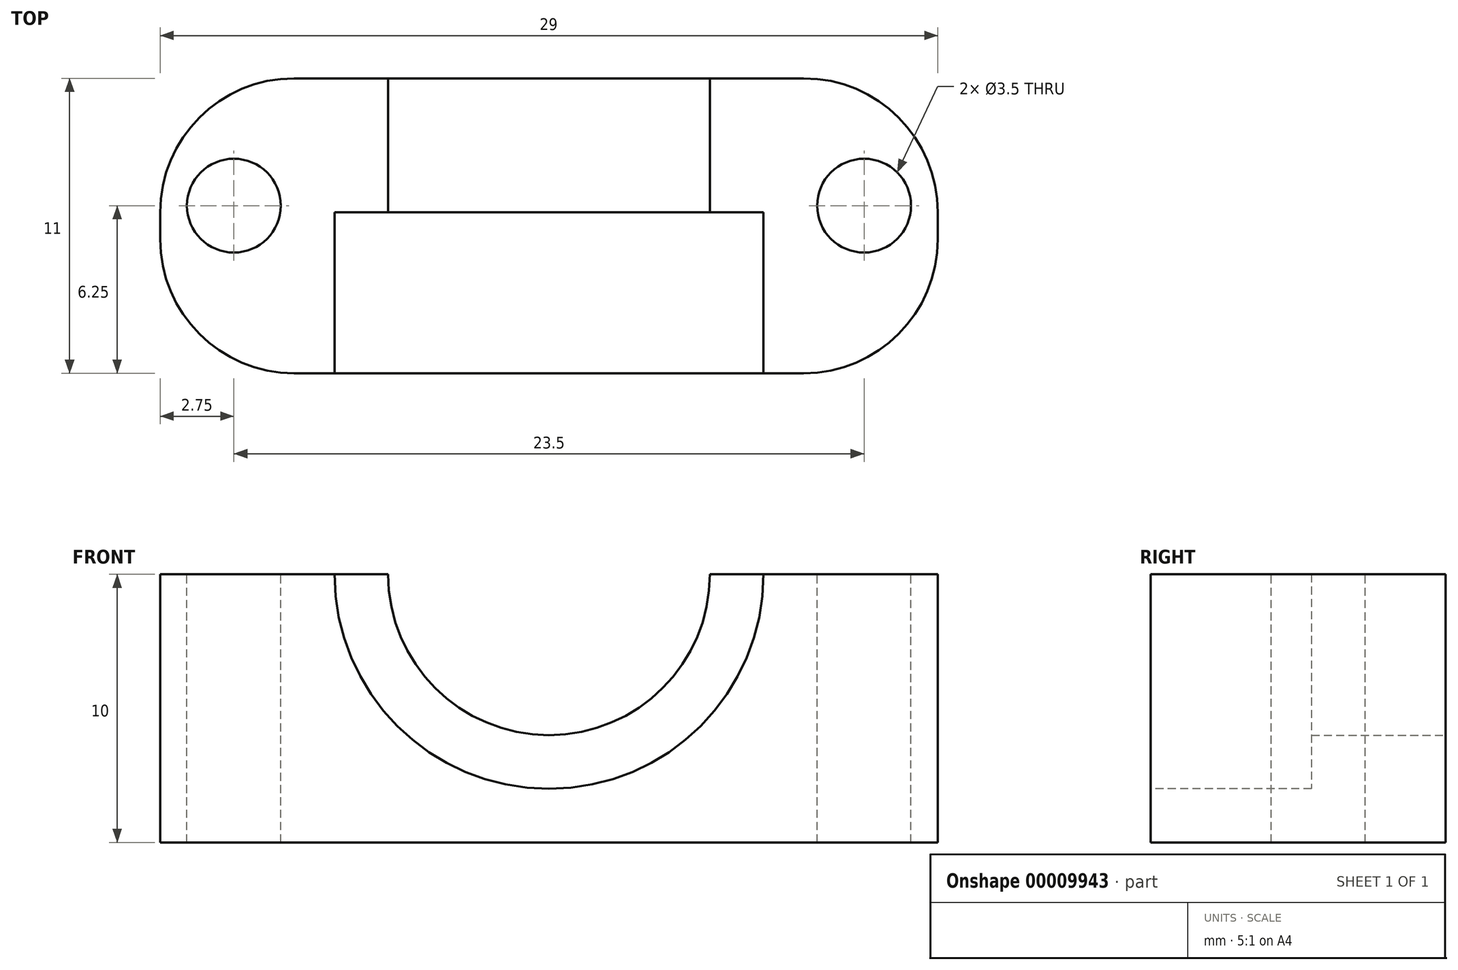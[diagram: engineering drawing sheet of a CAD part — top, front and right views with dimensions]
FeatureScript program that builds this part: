
annotation { "Feature Type Name" : "Feature", "Feature Type Description" : "" }
export const myFeature = defineFeature(function(context is Context, id is Id, definition is map)
    precondition{}
    {
        {
            var Q0;
            Q0=qCreatedBy(makeId("Top.planeOp"),FACE);
            var sketch = newSketch(context, id + "F0", { "sketchPlane" : qUnion([Q0])});
            skLineSegment(sketch, "E0.bottom", {"start": v(0, 0) * mm, "end": v(25, 0) * mm});
            skLineSegment(sketch, "E0.top", {"start": v(0, 11) * mm, "end": v(25, 11) * mm});
            skLineSegment(sketch, "E0.left", {"start": v(0, 0) * mm, "end": v(0, 11) * mm});
            skLineSegment(sketch, "E0.right", {"start": v(25, 0) * mm, "end": v(25, 11) * mm});
            skSolve(sketch);
        }
        {
            var Q0;
            Q0 = qSketchRegion(id + "F0", true);
            extrude(context, id + "F1", {"entities" : qUnion([Q0]), "depth" : 10 * mm});
        }
        {
            var Q0;
            Q0=makeQuery(id+"F1.opExtrude","SWEPT_FACE",FACE,{"disambiguationData":[OSD([sQuery(id+"F0.wireOp",EDGE,"E0.bottom")])]});
            var sketch = newSketch(context, id + "F2", { "sketchPlane" : qUnion([Q0])});
            skCircle(sketch, "E1", {"center": v(12.5, 10) * mm, "radius": 8 * mm});
            skSolve(sketch);
        }
        {
            var Q0;
            Q0 = qSketchRegion(id + "F2", true);
            extrude(context, id + "F3", {"entities" : qUnion([Q0]), "operationType" : NewBodyOperationType.REMOVE, "oppositeDirection" : true, "depth" : 6 * mm});
        }
        {
            var Q0;
            Q0=makeQuery(id+"F1.opExtrude","SWEPT_FACE",FACE,{"disambiguationData":[OSD([sQuery(id+"F0.wireOp",EDGE,"E0.top")])]});
            var sketch = newSketch(context, id + "F4", { "sketchPlane" : qUnion([Q0])});
            skCircle(sketch, "E2", {"center": v(-12.5, 10) * mm, "radius": 6 * mm});
            skSolve(sketch);
        }
        {
            var Q0;
            Q0 = qSketchRegion(id + "F4", true);
            extrude(context, id + "F5", {"entities" : qUnion([Q0]), "operationType" : NewBodyOperationType.REMOVE, "oppositeDirection" : true, "depth" : 6 * mm});
        }
        {
            var Q0;
            Q0=makeQuery(id+"F1.opExtrude","SWEPT_FACE",FACE,{"disambiguationData":[OSD([sQuery(id+"F0.wireOp",EDGE,"E0.left")])]});
            var sketch = newSketch(context, id + "F6", { "sketchPlane" : qUnion([Q0])});
            skLineSegment(sketch, "E3.bottom", {"start": v(-11, 0) * mm, "end": v(0, 0) * mm});
            skLineSegment(sketch, "E3.top", {"start": v(-11, 10) * mm, "end": v(0, 10) * mm});
            skLineSegment(sketch, "E3.left", {"start": v(-11, 0) * mm, "end": v(-11, 10) * mm});
            skLineSegment(sketch, "E3.right", {"start": v(0, 0) * mm, "end": v(0, 10) * mm});
            skSolve(sketch);
        }
        {
            var Q0;
            Q0 = qSketchRegion(id + "F6", true);
            extrude(context, id + "F7", {"entities" : qUnion([Q0]), "operationType" : NewBodyOperationType.ADD, "depth" : 2 * mm});
        }
        {
            var Q0;
            Q0=makeQuery(id+"F1.opExtrude","SWEPT_FACE",FACE,{"disambiguationData":[OSD([sQuery(id+"F0.wireOp",EDGE,"E0.right")])]});
            var sketch = newSketch(context, id + "F8", { "sketchPlane" : qUnion([Q0])});
            skLineSegment(sketch, "E4.bottom", {"start": v(11, 10) * mm, "end": v(0, 10) * mm});
            skLineSegment(sketch, "E4.top", {"start": v(11, 0) * mm, "end": v(0, 0) * mm});
            skLineSegment(sketch, "E4.left", {"start": v(11, 10) * mm, "end": v(11, 0) * mm});
            skLineSegment(sketch, "E4.right", {"start": v(0, 10) * mm, "end": v(0, 0) * mm});
            skSolve(sketch);
        }
        {
            var Q0;
            Q0 = qSketchRegion(id + "F8", true);
            extrude(context, id + "F9", {"entities" : qUnion([Q0]), "operationType" : NewBodyOperationType.ADD, "depth" : 2 * mm});
        }
        {
            var Q0;
            Q0=makeQuery(id+"F9.opExtrude","CAP_EDGE",EDGE,{"disambiguationData":[OSD([sQuery(id+"F8.wireOp",EDGE,"E4.left")])],"isStart":false});
            var Q1;
            Q1=makeQuery(id+"F9.opExtrude","CAP_EDGE",EDGE,{"disambiguationData":[OSD([sQuery(id+"F8.wireOp",EDGE,"E4.right")])],"isStart":false});
            var Q2;
            Q2=makeQuery(id+"F7.opExtrude","CAP_EDGE",EDGE,{"disambiguationData":[OSD([sQuery(id+"F6.wireOp",EDGE,"E3.left")])],"isStart":false});
            var Q3;
            Q3=makeQuery(id+"F7.opExtrude","CAP_EDGE",EDGE,{"disambiguationData":[OSD([sQuery(id+"F6.wireOp",EDGE,"E3.right")])],"isStart":false});
            fillet(context, id + "F10", {"entities" : qUnion([Q0, Q1, Q2, Q3]), "radius" : 5 * mm, "tangentPropagation" : true, "allowEdgeOverflow" : false});
        }
        {
            var Q0;
            {var subQ0=sQuery(id+"F0.wireOp",EDGE,"E0.bottom");var subQ1=sQuery(id+"F0.wireOp",EDGE,"E0.top");var subQ2=sQuery(id+"F0.wireOp",EDGE,"E0.left");Q0=makeQuery(id+"F5.boolean.opBoolean","SPLIT",FACE,{"disambiguationData":[TD([makeQuery(id+"F1.opExtrude","SWEPT_FACE",FACE,{"disambiguationData":[OSD([subQ2])]})])],"derivedFrom":makeQuery(id+"F1.opExtrude","CAP_FACE",FACE,{"disambiguationData":[OSD([subQ0,subQ1,subQ2,sQuery(id+"F0.wireOp",EDGE,"E0.right")])],"isStart":false})});}
            var sketch = newSketch(context, id + "F11", { "sketchPlane" : qUnion([Q0])});
            skCircle(sketch, "E5", {"center": v(0.75, 6.25) * mm, "radius": 1.75 * mm});
            skCircle(sketch, "E6", {"center": v(24.25, 6.25) * mm, "radius": 1.75 * mm});
            skSolve(sketch);
        }
        {
            var Q0;
            Q0 = qSketchRegion(id + "F11", true);
            extrude(context, id + "F12", {"entities" : qUnion([Q0]), "operationType" : NewBodyOperationType.REMOVE, "oppositeDirection" : true, "depth" : 25 * mm});
        }
    });
